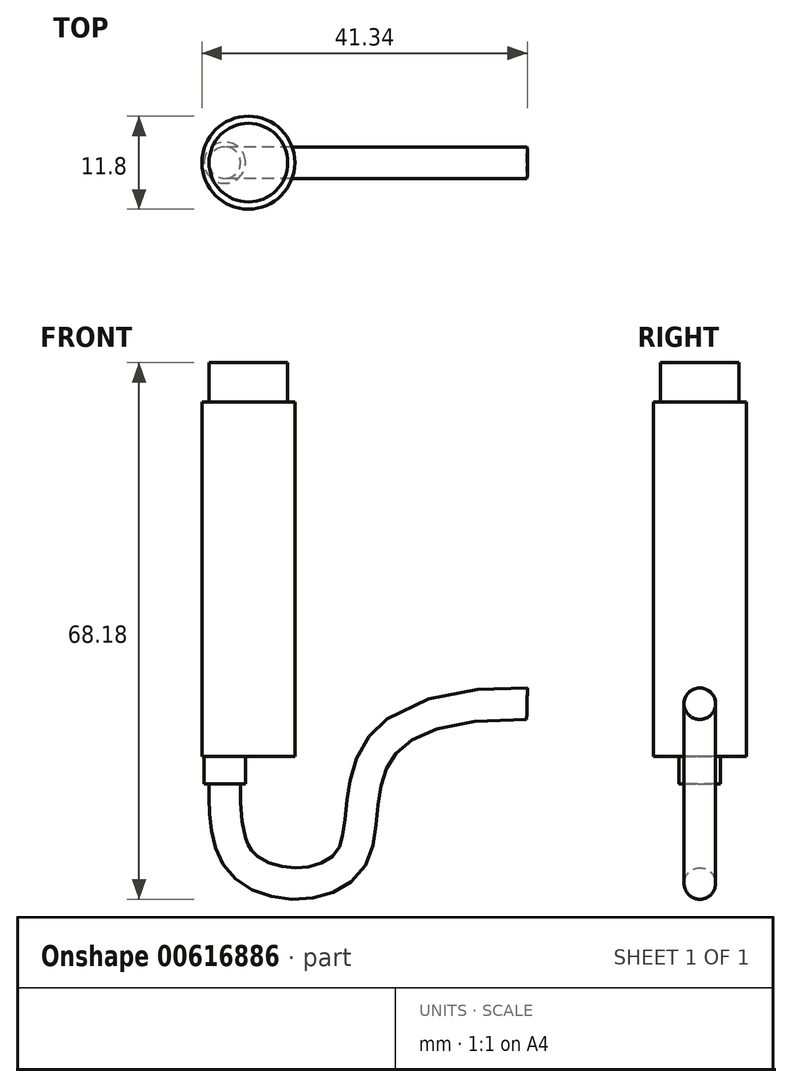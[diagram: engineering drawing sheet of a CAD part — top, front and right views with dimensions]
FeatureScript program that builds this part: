
annotation { "Feature Type Name" : "Feature", "Feature Type Description" : "" }
export const myFeature = defineFeature(function(context is Context, id is Id, definition is map)
    precondition{}
    {
        {
            var Q0;
            Q0=qCreatedBy(makeId("Top.planeOp"),FACE);
            var sketch = newSketch(context, id + "F0", { "sketchPlane" : qUnion([Q0])});
            skCircle(sketch, "E0", {"center": v(0, 0) * mm, "radius": 5.9 * mm});
            skSolve(sketch);
        }
        {
            var Q0;
            Q0=makeQuery(id+"F0.imprint","IMPRINT",FACE,{"disambiguationData":[TD([[makeQuery(id+"F0.imprint","IMPRINT",EDGE,{"derivedFrom":sQuery(id+"F0.wireOp",EDGE,"E0")}),1.0]])]});
            extrude(context, id + "F1", {"entities" : qUnion([Q0]), "depth" : 45 * mm, "offsetDistance" : 25 * mm});
        }
        {
            var Q0;
            Q0=makeQuery(id+"F1.opExtrude","CAP_FACE",FACE,{"disambiguationData":[OSD([sQuery(id+"F0.wireOp",EDGE,"E0")])],"isStart":true});
            var sketch = newSketch(context, id + "F2", { "sketchPlane" : qUnion([Q0])});
            skCircle(sketch, "E1", {"center": v(-3, 0) * mm, "radius": 2.62 * mm});
            skSolve(sketch);
        }
        {
            var Q0;
            Q0=makeQuery(id+"F2.imprint","IMPRINT",FACE,{"disambiguationData":[TD([[makeQuery(id+"F2.imprint","IMPRINT",EDGE,{"derivedFrom":sQuery(id+"F2.wireOp",EDGE,"E1")}),1.0]])]});
            extrude(context, id + "F3", {"entities" : qUnion([Q0]), "operationType" : NewBodyOperationType.ADD, "depth" : 3.5 * mm, "offsetDistance" : 25 * mm});
        }
        {
            var Q0;
            Q0=makeQuery(id+"F1.opExtrude","CAP_FACE",FACE,{"disambiguationData":[OSD([sQuery(id+"F0.wireOp",EDGE,"E0")])],"isStart":false});
            var sketch = newSketch(context, id + "F4", { "sketchPlane" : qUnion([Q0])});
            skCircle(sketch, "E2", {"center": v(0, 0) * mm, "radius": 5 * mm});
            skSolve(sketch);
        }
        {
            var Q0;
            Q0=makeQuery(id+"F4.imprint","IMPRINT",FACE,{"disambiguationData":[TD([[makeQuery(id+"F4.imprint","IMPRINT",EDGE,{"derivedFrom":sQuery(id+"F4.wireOp",EDGE,"E2")}),1.0]])]});
            extrude(context, id + "F5", {"entities" : qUnion([Q0]), "operationType" : NewBodyOperationType.ADD, "depth" : 5 * mm, "offsetDistance" : 25 * mm});
        }
        {
            var Q0;
            Q0=qCreatedBy(makeId("Front.planeOp"),FACE);
            var sketch = newSketch(context, id + "F6", { "sketchPlane" : qUnion([Q0])});
            skLineSegment(sketch, "E3.0", {"start": v(-0.37, -3.5) * mm, "end": v(-5.62, -3.5) * mm, "construction": true});
            skPoint(sketch, "E4.1.internal.snap0", {"position": v(-3, -3.5) * mm});
            skFitSpline(sketch, "E5", {"points": [v(-3, -3.5) * mm, v(0, -14.38) * mm, v(13.02, -13.04) * mm, v(35.4, 6.66) * mm], "startDerivative": vector(0.32, -40.11) * mm, "endDerivative": vector(179.73, -3) * mm});
            skSolve(sketch);
        }
        {
            var Q0;
            Q0=makeQuery(id+"F3.opExtrude","CAP_FACE",FACE,{"disambiguationData":[OSD([sQuery(id+"F2.wireOp",EDGE,"E1")])],"isStart":false});
            var sketch = newSketch(context, id + "F7", { "sketchPlane" : qUnion([Q0])});
            skCircle(sketch, "E6", {"center": v(-3, 0) * mm, "radius": 2 * mm});
            skSolve(sketch);
        }
        {
            var Q0;
            Q0 = qSketchRegion(id + "F7", true);
            var Q1;
            Q1=sQuery(id+"F6.wireOp",EDGE,"E5");
            sweep(context, id + "F8", {"operationType" : NewBodyOperationType.ADD, "profiles" : qUnion([Q0]), "path" : qUnion([Q1])});
        }
    });
